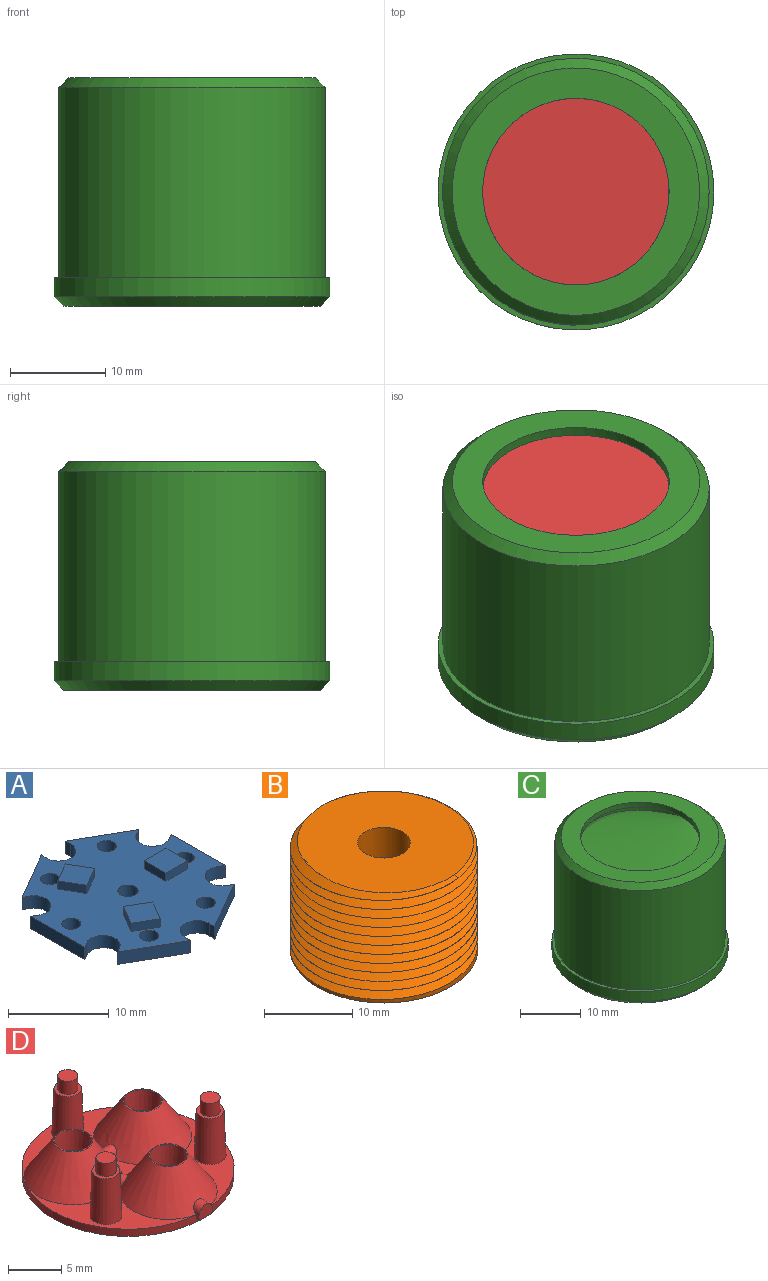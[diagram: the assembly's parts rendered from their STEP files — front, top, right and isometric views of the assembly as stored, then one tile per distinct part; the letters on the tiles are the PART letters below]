
ASSEMBLY  parts=4 mates=4
PART A: 48 faces, bbox 19.8x21x2.5 mm
  f0: cylinder r=1.69mm len=3.19mm, axis (0,0,-1), area 8.2mm2, adj f1,f30,f31,f32
  f1: plane 1.5x0.63mm, normal (-0.47,0.88,0), area 1.1mm2, adj f0,f2,f31,f32
  f2: plane 6.58x3.76mm, normal (-0.5,-0.87,0), area 11.4mm2, adj f1,f3,f31,f32
  f3: plane 1.5x0.71mm, normal (1,0.04,0), area 1.1mm2, adj f2,f4,f31,f32
  f4: cylinder r=1.69mm len=3.39mm, axis (0,0,-1), area 8.2mm2, adj f3,f5,f31,f32
  f5: plane 1.5x0.71mm, normal (-1,0.03,0), area 1.1mm2, adj f4,f6,f31,f32
  f6: plane 6.54x3.82mm, normal (0.5,-0.86,0), area 11.4mm2, adj f5,f7,f31,f32
  f7: plane 1.5x0.63mm, normal (0.47,0.88,0), area 1.1mm2, adj f6,f8,f31,f32
  f8: cylinder r=1.69mm len=3.2mm, axis (0,0,-1), area 8.2mm2, adj f7,f9,f31,f32
  f9: plane 1.5x0.61mm, normal (-0.53,-0.85,0), area 1.1mm2, adj f8,f10,f31,f32
  f10: plane 7.58x1.5mm, normal (1,0,0), area 11.4mm2, adj f9,f11,f31,f32
  f11: plane 1.5x0.6mm, normal (-0.53,0.85,0), area 1.1mm2, adj f10,f12,f31,f32
  f12: cylinder r=1.69mm len=3.19mm, axis (0,0,-1), area 8.2mm2, adj f11,f13,f31,f32
  f13: plane 1.5x0.63mm, normal (0.47,-0.88,0), area 1.1mm2, adj f12,f14,f31,f32
  f14: plane 6.58x3.76mm, normal (0.5,0.87,0), area 11.4mm2, adj f13,f15,f31,f32
  f15: plane 1.5x0.71mm, normal (-1,-0.04,0), area 1.1mm2, adj f14,f16,f31,f32
  f16: cylinder r=1.69mm len=3.39mm, axis (0,0,-1), area 8.2mm2, adj f15,f17,f31,f32
  f17: plane 1.5x0.71mm, normal (1,-0.03,0), area 1.1mm2, adj f16,f18,f31,f32
  f18: plane 6.54x3.82mm, normal (-0.5,0.86,0), area 11.4mm2, adj f17,f19,f31,f32
  f19: plane 1.5x0.63mm, normal (-0.47,-0.88,0), area 1.1mm2, adj f18,f20,f31,f32
  f20: cylinder r=1.69mm len=3.2mm, axis (0,0,-1), area 8.2mm2, adj f19,f21,f31,f32
  f21: plane 1.5x0.61mm, normal (0.53,0.85,0), area 1.1mm2, adj f20,f22,f31,f32
  f22: plane 7.58x1.5mm, normal (-1,0,0), area 11.4mm2, adj f21,f30,f31,f32
  f23: cylinder r=0.95mm len=1.9mm, axis (0,0,-1), area 9mm2, adj f31,f32
  f24: cylinder r=0.95mm len=1.9mm, axis (0,0,-1), area 9mm2, adj f31,f32
  f25: cylinder r=0.95mm len=1.9mm, axis (0,0,-1), area 9mm2, adj f31,f32
  f26: cylinder r=0.95mm len=1.9mm, axis (0,0,-1), area 9mm2, adj f31,f32
  f27: cylinder r=0.95mm len=1.9mm, axis (0,0,-1), area 9mm2, adj f31,f32
  f28: cylinder r=0.95mm len=1.9mm, axis (0,0,-1), area 9mm2, adj f31,f32
  f29: cylinder r=1mm len=2mm, axis (0,0,-1), area 9.4mm2, adj f31,f32
  f30: plane 1.5x0.6mm, normal (0.53,-0.85,0), area 1.1mm2, adj f0,f22,f31,f32
  f31: plane 20.95x19.83mm, normal (0,0,1), area 240mm2, adj f0,f1,f2,f3,f4,f5,f6,f7
  f32: plane 20.95x19.83mm, normal (0,0,-1), area 267mm2, adj f0,f1,f2,f3,f4,f5,f6,f7
  f33: plane 3x1mm, normal (0,1,0), area 3mm2, adj f31,f34,f36,f37
  f34: plane 3x1mm, normal (-1,0,0), area 3mm2, adj f31,f33,f35,f37
  f35: plane 3x1mm, normal (0,-1,0), area 3mm2, adj f31,f34,f36,f37
  f36: plane 3x1mm, normal (1,0,0), area 3mm2, adj f31,f33,f35,f37
  f37: plane 3x3mm, normal (0,0,1), area 9mm2, adj f33,f34,f35,f36
  f38: plane 2.6x1.5mm, normal (-0.87,-0.5,0), area 3mm2, adj f31,f39,f41,f42
  f39: plane 2.6x1.5mm, normal (0.5,-0.87,0), area 3mm2, adj f31,f38,f40,f42
  f40: plane 2.6x1.5mm, normal (0.87,0.5,0), area 3mm2, adj f31,f39,f41,f42
  f41: plane 2.6x1.5mm, normal (-0.5,0.87,0), area 3mm2, adj f31,f38,f40,f42
  f42: plane 4.1x4.1mm, normal (0,0,1), area 9mm2, adj f38,f39,f40,f41
  f43: plane 2.6x1.5mm, normal (0.87,-0.5,0), area 3mm2, adj f31,f44,f46,f47
  f44: plane 2.6x1.5mm, normal (0.5,0.87,0), area 3mm2, adj f31,f43,f45,f47
  f45: plane 2.6x1.5mm, normal (-0.87,0.5,0), area 3mm2, adj f31,f44,f46,f47
  f46: plane 2.6x1.5mm, normal (-0.5,-0.87,0), area 3mm2, adj f31,f43,f45,f47
  f47: plane 4.1x4.1mm, normal (0,0,1), area 9mm2, adj f43,f44,f45,f46
PART B: 21 faces, bbox 21.6x24.9x16.2 mm
  f0: cylinder r=10.65mm len=21.3mm, axis (0,0,-1), area 70mm2, adj f4,f5,f6,f7,f8
  f1: cylinder r=3mm len=15mm, axis (0,0,-1), area 282.7mm2, adj f2,f3
  f2: plane 20.56x20.05mm, normal (0,0,1), area 285.1mm2, adj f1,f5,f7,f8
  f3: plane 20.3x20.3mm, normal (0,0,-1), area 237.7mm2, adj f1,f4,f9,f11,f13,f15,f17,f19
  f4: cone r=10.65mm half-angle=60deg, axis (0,0,1), area 35.5mm2, adj f0,f3,f6,f8
  f5: cone r=10.15mm half-angle=60deg, axis (0,0,-1), area 8.6mm2, adj f0,f2,f7,f8
  f6: plane 1.11x1.1mm, normal (0,1,0), area 0.7mm2, adj f0,f4,f7,f8
  f7: bspline ~24.6x21.3mm, area 897.2mm2, adj f0,f2,f5,f6,f8
  f8: bspline ~24.6x21.3mm, area 938.4mm2, adj f0,f2,f4,f5,f6,f7
  f9: cylinder r=1.75mm len=10mm, axis (0,0,-1), area 110mm2, adj f3,f10
  f10: plane 3.5x3.5mm, normal (0,0,-1), area 9.6mm2, adj f9
  f11: cylinder r=1.75mm len=10mm, axis (0,0,-1), area 110mm2, adj f3,f12
  f12: plane 3.5x3.5mm, normal (0,0,-1), area 9.6mm2, adj f11
  f13: cylinder r=1.75mm len=10mm, axis (0,0,-1), area 110mm2, adj f3,f14
  f14: plane 3.5x3.5mm, normal (0,0,-1), area 9.6mm2, adj f13
  f15: cylinder r=1.75mm len=10mm, axis (0,0,-1), area 110mm2, adj f3,f16
  f16: plane 3.5x3.5mm, normal (0,0,-1), area 9.6mm2, adj f15
  f17: cylinder r=1.75mm len=10mm, axis (0,0,-1), area 110mm2, adj f3,f18
  f18: plane 3.5x3.5mm, normal (0,0,-1), area 9.6mm2, adj f17
  f19: cylinder r=1.75mm len=10mm, axis (0,0,-1), area 110mm2, adj f3,f20
  f20: plane 3.5x3.5mm, normal (0,0,-1), area 9.6mm2, adj f19
PART C: 15 faces, bbox 29x29x24.3 mm
  f0: cylinder r=14.5mm len=29mm, axis (0,0,-1), area 182.2mm2, adj f1,f14
  f1: plane 29x29mm, normal (0,0,1), area 44.8mm2, adj f0,f3
  f2: plane 27x27mm, normal (0,0,-1), area 187.1mm2, adj f8,f14
  f3: cylinder r=14mm len=28mm, axis (0,0,-1), area 1759.3mm2, adj f1,f13
  f4: plane 26x26mm, normal (0,0,1), area 229.2mm2, adj f7,f13
  f5: cylinder r=10.5mm len=22mm, axis (0,0,-1), area 111.6mm2, adj f6,f8,f9,f11,f12
  f6: plane 21x21mm, normal (0,0,-1), area 44.6mm2, adj f5,f7
  f7: cylinder r=9.8mm len=19.6mm, axis (0,0,-1), area 61.6mm2, adj f4,f6
  f8: cone r=10.5mm half-angle=30deg, axis (0,0,-1), area 42.3mm2, adj f2,f5,f10,f12
  f9: plane 1.24x1.1mm, normal (0,-1,0), area 0.7mm2, adj f5,f11,f12
  f10: plane 0.94x0.89mm, normal (-0.59,-0.81,0), area 0.3mm2, adj f8,f11,f12
  f11: bspline ~23.19x23.18mm, area 1550.2mm2, adj f5,f9,f10,f12
  f12: bspline ~26.79x23.2mm, area 1524.3mm2, adj f5,f8,f9,f10,f11
  f13: cone r=13mm half-angle=45deg, axis (0,0,-1), area 120mm2, adj f3,f4
  f14: cone r=14.5mm half-angle=45deg, axis (0,0,1), area 124.4mm2, adj f0,f2
PART D: 44 faces, bbox 20x20.3x7.5 mm
  f0: plane 3.34x3.34mm, normal (0,0,1), area 8.7mm2, adj f5
  f1: plane 3.34x3.34mm, normal (0,0,1), area 8.7mm2, adj f6
  f2: plane 1.9x1.9mm, normal (0,0,1), area 2.8mm2, adj f7
  f3: plane 1.9x1.9mm, normal (0,0,1), area 2.8mm2, adj f8
  f4: plane 1.9x1.9mm, normal (0,0,1), area 2.8mm2, adj f9
  f5: cone r=0mm half-angle=2deg, axis (0,0,1), area 25.2mm2, adj f0,f11
  f6: cone r=0mm half-angle=2deg, axis (0,0,1), area 25.2mm2, adj f1,f13
  f7: cylinder r=0.95mm len=1.9mm, axis (0,0,1), area 9mm2, adj f2,f17
  f8: cylinder r=0.95mm len=1.9mm, axis (0,0,1), area 9mm2, adj f3,f18
  f9: cylinder r=0.95mm len=1.9mm, axis (0,0,1), area 9mm2, adj f4,f19
  f10: plane 3.34x3.34mm, normal (0,0,1), area 8.7mm2, adj f22
  f11: plane 3.7x3.7mm, normal (0,0,1), area 1.1mm2, adj f5,f30
  f12: plane 0.48x0.25mm, normal (0,1,0), area 0.1mm2, adj f14,f30,f31,f40
  f13: plane 3.7x3.7mm, normal (0,0,1), area 1.1mm2, adj f6,f31
  f14: cylinder r=0.75mm len=1.5mm, axis (1,0,0), area 2.5mm2, adj f12,f15,f30,f31
  f15: plane 0.48x0.25mm, normal (0,-1,0), area 0.1mm2, adj f14,f29,f30,f31
  f16: plane 19.91x19.91mm, normal (0,0,-1), area 311.4mm2, adj f32
  f17: plane 2.64x2.64mm, normal (0,0,1), area 2.6mm2, adj f7,f33
  f18: plane 2.64x2.64mm, normal (0,0,1), area 2.6mm2, adj f8,f34
  f19: plane 2.64x2.64mm, normal (0,0,1), area 2.6mm2, adj f9,f35
  f20: plane 1.62x0.41mm, normal (0,0,-1), area 0.6mm2, adj f21,f32,f36,f37
  f21: plane 0.5x0.41mm, normal (-0.98,0,-0.17), area 0.2mm2, adj f20,f32,f37,f38
  f22: cone r=0mm half-angle=2deg, axis (0,0,1), area 25.2mm2, adj f10,f39
  f23: plane 0.42x0.25mm, normal (-0.87,0.5,0), area 0.1mm2, adj f24,f29,f30,f43
  f24: cylinder r=0.75mm len=1.98mm, axis (-0.5,-0.87,0), area 2.5mm2, adj f23,f25,f30,f43
  f25: plane 0.42x0.25mm, normal (0.87,-0.5,0), area 0.1mm2, adj f24,f30,f40,f43
  f26: plane 0.42x0.25mm, normal (-0.87,-0.5,0), area 0.1mm2, adj f27,f31,f40,f43
  f27: cylinder r=0.75mm len=1.98mm, axis (0.5,-0.87,0), area 2.5mm2, adj f26,f28,f31,f43
  f28: plane 0.42x0.25mm, normal (0.87,0.5,0), area 0.1mm2, adj f27,f29,f31,f43
  f29: plane 3.4x2.94mm, normal (0,0,1), area 3.5mm2, adj f15,f23,f28,f30,f31,f43
  f30: cone r=0mm half-angle=33.7deg, axis (0,0,-1), area 98.3mm2, adj f11,f12,f14,f15,f23,f24,f25,f29
  f31: cone r=0mm half-angle=33.7deg, axis (0,0,-1), area 98.3mm2, adj f12,f13,f14,f15,f26,f27,f28,f29
  f32: cone r=0mm half-angle=2deg, axis (0,0,1), area 52.4mm2, adj f16,f20,f21,f36,f40
  f33: cone r=0mm half-angle=2deg, axis (0,0,-1), area 45.7mm2, adj f17,f40
  f34: cone r=0mm half-angle=2deg, axis (0,0,-1), area 45.7mm2, adj f18,f40
  f35: cone r=0mm half-angle=2deg, axis (0,0,-1), area 45.7mm2, adj f19,f40
  f36: plane 0.5x0.41mm, normal (0.98,0,-0.17), area 0.2mm2, adj f20,f32,f37,f41
  f37: plane 1.8x1.5mm, normal (0,-1,0), area 2.3mm2, adj f20,f21,f36,f38,f41,f42
  f38: plane 0.66x0.29mm, normal (-0.98,0,0.17), area 0.2mm2, adj f21,f37,f40,f42,f43
  f39: plane 3.7x3.7mm, normal (0,0,1), area 1.1mm2, adj f22,f43
  f40: plane 19.97x19.93mm, normal (0,0,1), area 87.5mm2, adj f12,f25,f26,f30,f31,f32,f33,f34
  f41: plane 0.66x0.29mm, normal (0.98,0,0.17), area 0.2mm2, adj f36,f37,f40,f42,f43
  f42: cylinder r=0.86mm len=1.7mm, axis (0,1,0), area 2.2mm2, adj f37,f38,f41,f43
  f43: cone r=0mm half-angle=33.7deg, axis (0,0,-1), area 96.5mm2, adj f23,f24,f25,f26,f27,f28,f29,f38
PLACE A rot(axis=(0,0,-1),30.3deg) t=(0,0,47.7)mm
PLACE B rot(axis=(0,0,-1),30.3deg) t=(0,0,32.7)mm
PLACE C t=(0,0,32.2)mm
PLACE D rot(axis=(1,0,0),180deg) t=(0,5.34,55.05)mm
MATE revolute D.f9 <-> A.f27  axis (0,0,-1) through (0,-8,49.2)mm
MATE fastened A.f29 <-> B.f1  axis (0,0,-1) through (0,0,47.7)mm
MATE fastened D.f32 <-> C.f5  axis (0,0,1) through (0,0,55.2)mm
MATE revolute D.f7 <-> A.f23  axis (0,0,-1) through (6.93,4,49.2)mm
